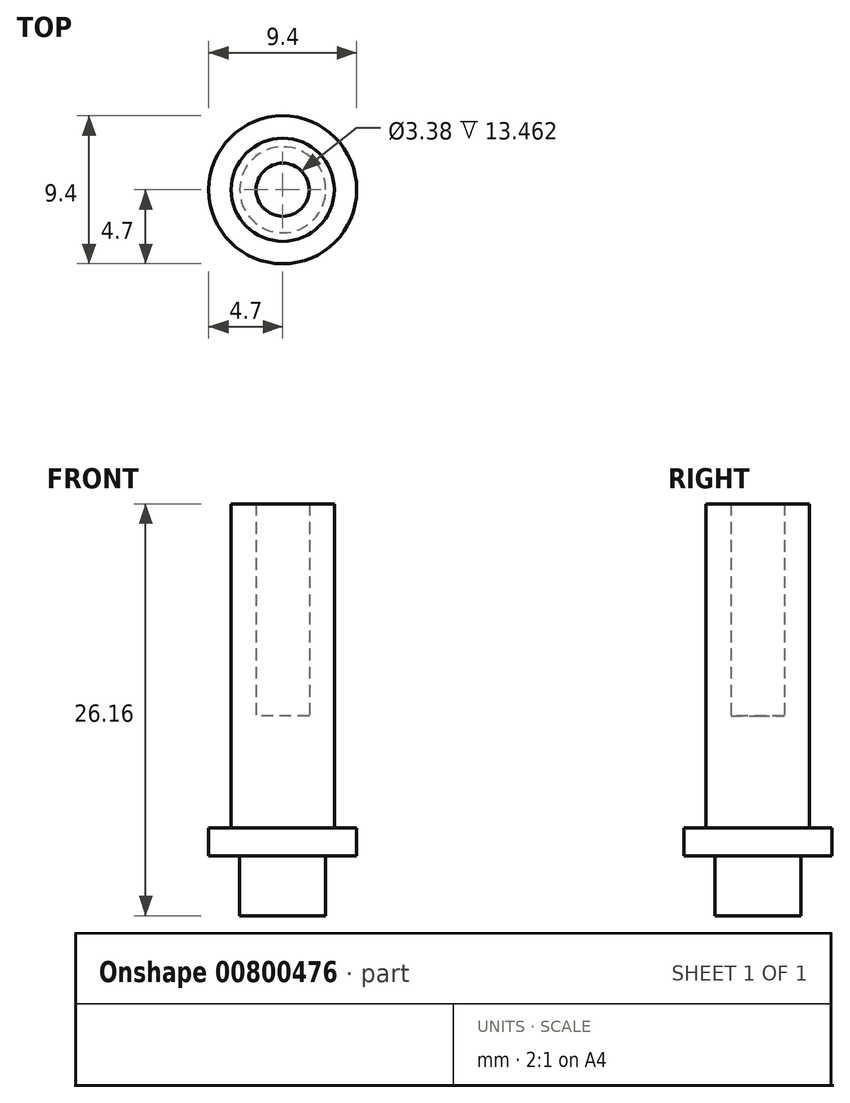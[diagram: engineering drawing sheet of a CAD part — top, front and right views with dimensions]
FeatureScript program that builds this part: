
annotation { "Feature Type Name" : "Feature", "Feature Type Description" : "" }
export const myFeature = defineFeature(function(context is Context, id is Id, definition is map)
    precondition{}
    {
        {
            var Q0;
            Q0=qCreatedBy(makeId("Top.planeOp"),FACE);
            var sketch = newSketch(context, id + "F0", { "sketchPlane" : qUnion([Q0])});
            skCircle(sketch, "E0", {"center": v(0, 0) * mm, "radius": 3.28 * mm});
            skSolve(sketch);
        }
        {
            var Q0;
            Q0 = qSketchRegion(id + "F0", true);
            extrude(context, id + "F1", {"entities" : qUnion([Q0]), "depth" : 8.9 * mm, "offsetDistance" : 25.4 * mm});
        }
        {
            var Q0;
            Q0=qCreatedBy(makeId("Top.planeOp"),FACE);
            var sketch = newSketch(context, id + "F2", { "sketchPlane" : qUnion([Q0])});
            skCircle(sketch, "E1", {"center": v(0, 0) * mm, "radius": 4.7 * mm});
            skSolve(sketch);
        }
        {
            var Q0;
            Q0 = qSketchRegion(id + "F2", true);
            extrude(context, id + "F3", {"entities" : qUnion([Q0]), "operationType" : NewBodyOperationType.ADD, "depth" : 1.78 * mm, "offsetDistance" : 25.4 * mm});
        }
        {
            var Q0;
            Q0=makeQuery(id+"F3.boolean.opBoolean","MERGE",FACE,{"derivedFrom":[makeQuery(id+"F1.opExtrude","CAP_FACE",FACE,{"disambiguationData":[OSD([sQuery(id+"F0.wireOp",EDGE,"E0")])],"isStart":true}),makeQuery(id+"F3.opExtrude","CAP_FACE",FACE,{"disambiguationData":[OSD([sQuery(id+"F2.wireOp",EDGE,"E1")])],"isStart":true})]});
            var sketch = newSketch(context, id + "F4", { "sketchPlane" : qUnion([Q0])});
            skCircle(sketch, "E2", {"center": v(0, 0) * mm, "radius": 2.73 * mm});
            skSolve(sketch);
        }
        {
            var Q0;
            Q0 = qSketchRegion(id + "F4", true);
            extrude(context, id + "F5", {"entities" : qUnion([Q0]), "operationType" : NewBodyOperationType.ADD, "depth" : 3.8 * mm, "offsetDistance" : 25.4 * mm});
        }
        {
            var Q0;
            Q0=makeQuery(id+"F1.opExtrude","CAP_FACE",FACE,{"disambiguationData":[OSD([sQuery(id+"F0.wireOp",EDGE,"E0")])],"isStart":false});
            var sketch = newSketch(context, id + "F6", { "sketchPlane" : qUnion([Q0])});
            skCircle(sketch, "E3", {"center": v(0, 0) * mm, "radius": 1.69 * mm});
            skSolve(sketch);
        }
        {
            var Q0;
            Q0=makeQuery(id+"F6.imprint","IMPRINT",FACE,{"disambiguationData":[TD([[makeQuery(id+"F6.imprint","IMPRINT",EDGE,{"derivedFrom":sQuery(id+"F6.wireOp",EDGE,"E3")}),-1.0]])]});
            extrude(context, id + "F7", {"entities" : qUnion([Q0]), "operationType" : NewBodyOperationType.ADD, "depth" : 13.46 * mm, "offsetDistance" : 25.4 * mm});
        }
    });
